# Revit family: IS_CeraPlusS_BC112_BIM_DE
name_source: partatom
category: Plumbing Fixtures
units: mm (PartAtom-declared; Revit-internal decimal feet)

## family parameters
Always vertical = Yes
Cut with Voids When Loaded = No
OmniClass Number = 23.45.55.17
OmniClass Title = Mixing Faucets
Part Type = Normal
Room Calculation Point = No
Round Connector Dimension = Use Diameter
Shared = No
Work Plane-Based = No

## types (1)
- BC112AA - CERAPLUS BASIN MIXER EXPOSED SPOUT/200 S/ON-OFF - CHROME
    Accessories = www.idealspec.co.uk
    AreaUnits = millimeters
    Assembly Code = C1030200
    AssetType = Fixed
    BIMObjectName = IS_IdealStandard_Washbasintaps_CeraPlusS_BC112
    BarCode = 3800861059684
    Brand = Ideal Standard
    Category = Taps & Mixers
    Color = Chromium Plated
    ConnectionType = Plumbing
    Cost = 0 $
    Description = CERAPLUS BASIN MIXER EXPOSED SPOUT/200 S/ON-OFF - CHROME
    DurationUnit = year
    FaucetType = Tap Mixer
    Features = BASIN MIXER EXPOSED SPOUT/200 S/ON-OFF - CHROME
    Finish = Chromium Plated
    Help = www.idealstandard.de
    IfcExportAs = IfcValveType
    IfcExportType = BASIN MIXER
    InstallationInstructions = www.idealstandard.de
    LinearUnits = millimeters
    MainColor = Chromium Plated
    MaintenanceInformation = www.idealstandard.de
    Manufacturer = www.idealstandard.de
    ManufacturerURL = www.idealstandard.de
    Model = BC112AA
    ModelNumber = BC112AA
    ModelReference = CERAPLUS BASIN MIXER EXPOSED SPOUT/200 S/ON-OFF
    Name = Washbasintaps_CeraPlusS_BC112_IdealStandard
    NettWeight = 0,00 KG
    NominalDepth = 0 mm  [stored 0 ft]
    NominalHeight = 0 mm  [stored 0 ft]
    NominalLength = 0 mm  [stored 0 ft]
    NominalWidth = 0 mm  [stored 0 ft]
    ProductInformation = www.idealstandard.de
    Shape = Sculptured
    Size = 0 x 0 x 0 mm
    Space = Internal
    SpareParts = www.idealstandard.de
    TestPressure = 10 bar
    URL = www.idealstandard.de
    Uniclass2015Code = Pr_40_20_87_98
    Uniclass2015Title = Washbasin taps
    Uniclass2015Version = Products v1.1

note: [stored X ft] marks values corroborated as IEEE doubles in the binary element streams (Revit-internal decimal feet)
